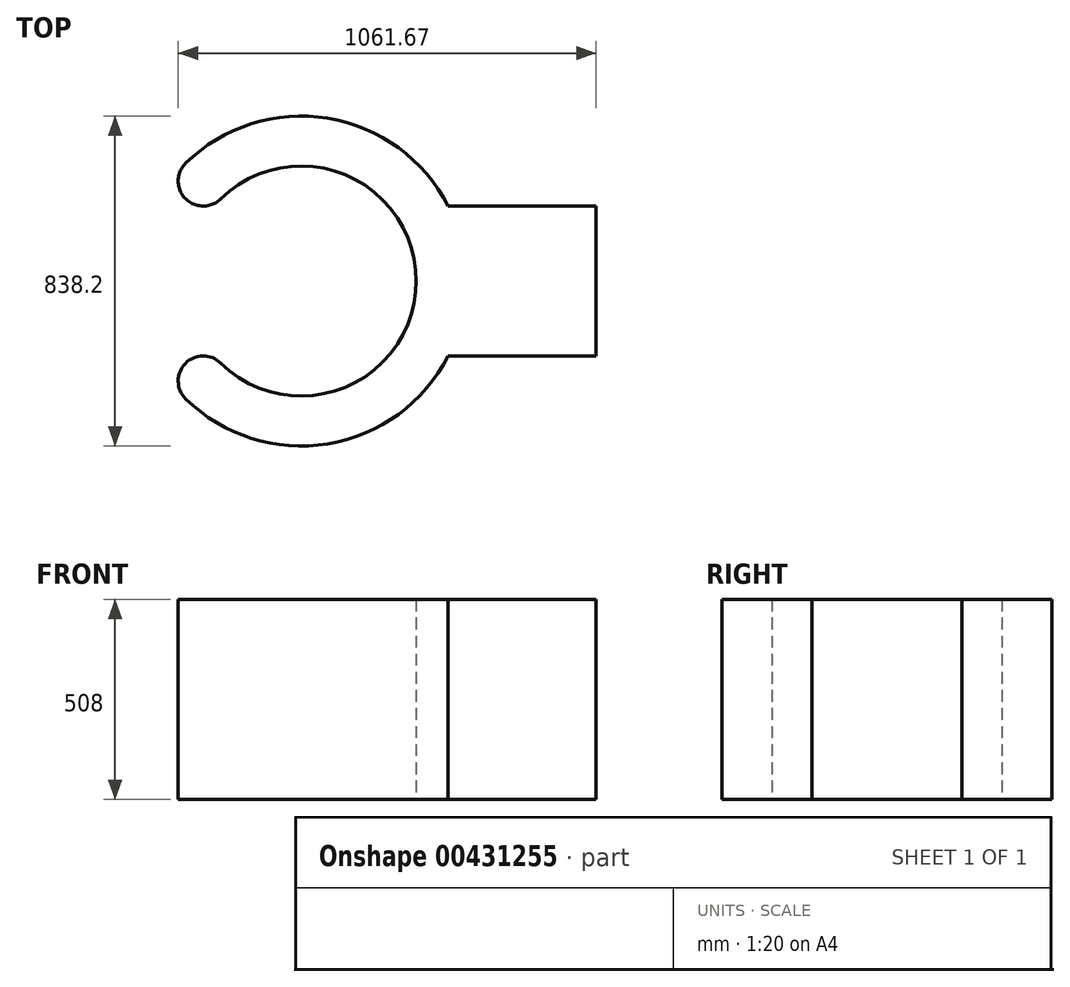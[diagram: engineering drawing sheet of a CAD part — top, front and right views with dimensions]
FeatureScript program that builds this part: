
annotation { "Feature Type Name" : "Feature", "Feature Type Description" : "" }
export const myFeature = defineFeature(function(context is Context, id is Id, definition is map)
    precondition{}
    {
        {
            var Q0;
            Q0=qCreatedBy(makeId("Top.planeOp"),FACE);
            var sketch = newSketch(context, id + "F0", { "sketchPlane" : qUnion([Q0])});
            skArc(sketch, "E0", {"start": v(-204.43, -208.64) * mm, "mid": v(292.1, 0) * mm, "end": v(-204.43, 208.64) * mm});
            skArc(sketch, "E1", {"start": v(-293.3, -299.36) * mm, "mid": v(67.54, -413.62) * mm, "end": v(373.3, -190.5) * mm});
            skArc(sketch, "E2", {"start": v(-293.3, 299.36) * mm, "mid": v(-294.23, 209.56) * mm, "end": v(-204.43, 208.64) * mm});
            skLineSegment(sketch, "E3", {"start": v(0, 0) * mm, "end": v(419.1, 0) * mm, "construction": true});
            skLineSegment(sketch, "E4", {"start": v(0, 0) * mm, "end": v(-450.54, 0) * mm, "construction": true});
            skArc(sketch, "E5.MirrorC", {"start": v(-293.3, -299.36) * mm, "mid": v(-294.23, -209.56) * mm, "end": v(-204.43, -208.64) * mm});
            skLineSegment(sketch, "E6.top", {"start": v(419.1, 190.5) * mm, "end": v(749.3, 190.5) * mm});
            skLineSegment(sketch, "E6.right", {"start": v(749.3, 0) * mm, "end": v(749.3, 190.5) * mm});
            skLineSegment(sketch, "E7.MirrorCS", {"start": v(749.3, 0) * mm, "end": v(749.3, -190.5) * mm});
            skLineSegment(sketch, "E8.MirrorCS", {"start": v(419.1, -190.5) * mm, "end": v(749.3, -190.5) * mm});
            skLineSegment(sketch, "E9", {"start": v(373.3, 190.5) * mm, "end": v(419.1, 190.5) * mm});
            skLineSegment(sketch, "E10.MirrorCS", {"start": v(373.3, -190.5) * mm, "end": v(419.1, -190.5) * mm});
            skArc(sketch, "E11.trimOffspring", {"start": v(373.3, 190.5) * mm, "mid": v(67.54, 413.62) * mm, "end": v(-293.3, 299.36) * mm});
            skPoint(sketch, "E12.MirrorCS.end.orphan", {"position": v(419.1, -190.5) * mm});
            skPoint(sketch, "E6.bottom.start.orphan", {"position": v(419.1, 0) * mm});
            skSolve(sketch);
        }
        {
            var Q0;
            Q0=makeQuery(id+"F0.imprint","IMPRINT",FACE,{"disambiguationData":[TD([[makeQuery(id+"F0.imprint","IMPRINT",EDGE,{"derivedFrom":sQuery(id+"F0.wireOp",EDGE,"E0")}),-1.0]])]});
            extrude(context, id + "F1", {"entities" : qUnion([Q0]), "depth" : 508 * mm});
        }
    });
